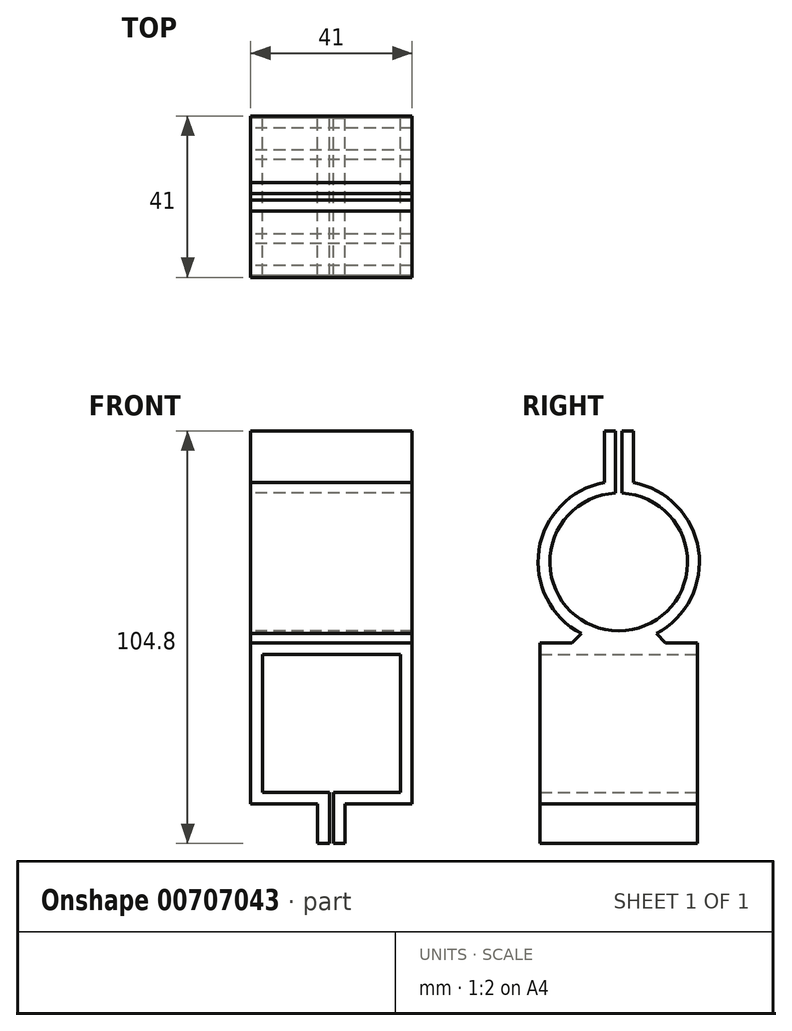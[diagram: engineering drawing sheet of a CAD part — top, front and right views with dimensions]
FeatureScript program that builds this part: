
annotation { "Feature Type Name" : "Feature", "Feature Type Description" : "" }
export const myFeature = defineFeature(function(context is Context, id is Id, definition is map)
    precondition{}
    {
        {
            var Q0;
            Q0=qCreatedBy(makeId("Front.planeOp"),FACE);
            var sketch = newSketch(context, id + "F0", { "sketchPlane" : qUnion([Q0])});
            skLineSegment(sketch, "E0.bottom", {"start": v(17.5, -38) * mm, "end": v(0.5, -38) * mm});
            skLineSegment(sketch, "E0.top", {"start": v(17.5, -3) * mm, "end": v(-17.5, -3) * mm});
            skLineSegment(sketch, "E0.left", {"start": v(17.5, -38) * mm, "end": v(17.5, -3) * mm});
            skLineSegment(sketch, "E0.right", {"start": v(-17.5, -38) * mm, "end": v(-17.5, -3) * mm});
            skPoint(sketch, "E0.middle", {"position": v(0, -20.5) * mm});
            skLineSegment(sketch, "E1.bottom", {"start": v(20.5, -41) * mm, "end": v(3.5, -41) * mm});
            skLineSegment(sketch, "E1.top", {"start": v(20.5, 0) * mm, "end": v(-20.5, 0) * mm});
            skLineSegment(sketch, "E1.left", {"start": v(20.5, -41) * mm, "end": v(20.5, 0) * mm});
            skLineSegment(sketch, "E1.right", {"start": v(-20.5, -41) * mm, "end": v(-20.5, 0) * mm});
            skLineSegment(sketch, "E2", {"start": v(-0.5, -38) * mm, "end": v(-0.5, -51) * mm});
            skLineSegment(sketch, "E3", {"start": v(-0.5, -51) * mm, "end": v(-3.5, -51) * mm});
            skLineSegment(sketch, "E4", {"start": v(-3.5, -51) * mm, "end": v(-3.5, -41) * mm});
            skLineSegment(sketch, "E5", {"start": v(0.5, -38) * mm, "end": v(0.5, -51) * mm});
            skLineSegment(sketch, "E6", {"start": v(0.5, -51) * mm, "end": v(3.5, -51) * mm});
            skLineSegment(sketch, "E7", {"start": v(3.5, -51) * mm, "end": v(3.5, -41) * mm});
            skLineSegment(sketch, "E8.trimOffspring", {"start": v(-0.5, -38) * mm, "end": v(-17.5, -38) * mm});
            skLineSegment(sketch, "E9.trimOffspring", {"start": v(-3.5, -41) * mm, "end": v(-20.5, -41) * mm});
            skSolve(sketch);
        }
        {
            var Q0;
            Q0 = qSketchRegion(id + "F0", true);
            extrude(context, id + "F1", {"entities" : qUnion([Q0]), "endBound" : BoundingType.SYMMETRIC, "depth" : 40 * mm, "offsetDistance" : 25 * mm});
        }
        {
            var Q0;
            Q0=qCreatedBy(makeId("Right.planeOp"),FACE);
            var sketch = newSketch(context, id + "F2", { "sketchPlane" : qUnion([Q0])});
            skArc(sketch, "E10", {"start": v(-0.82, 37.98) * mm, "mid": v(0, 3) * mm, "end": v(0.82, 37.98) * mm});
            skArc(sketch, "E11", {"start": v(-0.82, 40.98) * mm, "mid": v(0, 0) * mm, "end": v(0.82, 40.98) * mm});
            skLineSegment(sketch, "E12", {"start": v(-9.5, 2.34) * mm, "end": v(-11.84, 0) * mm});
            skLineSegment(sketch, "E13", {"start": v(-11.84, 0) * mm, "end": v(11.84, 0) * mm});
            skLineSegment(sketch, "E14", {"start": v(11.84, 0) * mm, "end": v(9.5, 2.34) * mm});
            skLineSegment(sketch, "E15.top", {"start": v(3.67, 53.8) * mm, "end": v(0.82, 53.8) * mm});
            skLineSegment(sketch, "E15.left", {"start": v(3.67, 37.61) * mm, "end": v(3.67, 53.8) * mm});
            skLineSegment(sketch, "E15.right", {"start": v(-3.67, 37.61) * mm, "end": v(-3.67, 53.8) * mm});
            skPoint(sketch, "E15.middle", {"position": v(0, 45.7) * mm});
            skLineSegment(sketch, "E16.left", {"start": v(0.82, 37.98) * mm, "end": v(0.82, 53.8) * mm});
            skLineSegment(sketch, "E16.right", {"start": v(-0.82, 37.98) * mm, "end": v(-0.82, 53.8) * mm});
            skLineSegment(sketch, "E17.trimOffspring", {"start": v(-0.82, 53.8) * mm, "end": v(-3.67, 53.8) * mm});
            skPoint(sketch, "E18.orphan", {"position": v(0.82, 56.23) * mm});
            skPoint(sketch, "E19.orphan", {"position": v(-0.82, 56.23) * mm});
            skPoint(sketch, "E20.orphan", {"position": v(0.82, 35.19) * mm});
            skPoint(sketch, "E21.orphan", {"position": v(-0.82, 35.19) * mm});
            skSolve(sketch);
        }
        {
            var Q0;
            Q0 = qSketchRegion(id + "F2", true);
            extrude(context, id + "F3", {"entities" : qUnion([Q0]), "operationType" : NewBodyOperationType.ADD, "endBound" : BoundingType.SYMMETRIC, "depth" : 41 * mm, "offsetDistance" : 25 * mm});
        }
    });
